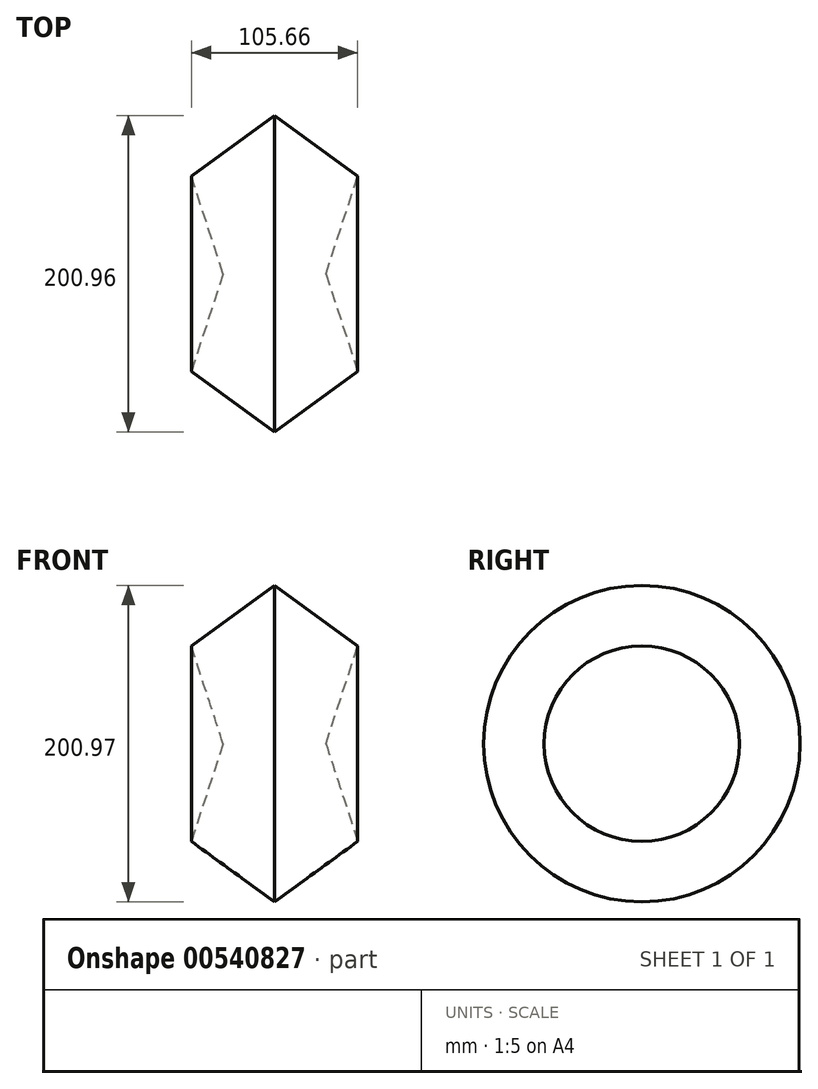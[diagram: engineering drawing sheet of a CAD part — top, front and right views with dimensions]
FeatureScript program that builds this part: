
annotation { "Feature Type Name" : "Feature", "Feature Type Description" : "" }
export const myFeature = defineFeature(function(context is Context, id is Id, definition is map)
    precondition{}
    {
        {
            var Q0;
            Q0=qCreatedBy(makeId("Front.planeOp"),FACE);
            var sketch = newSketch(context, id + "F0", { "sketchPlane" : qUnion([Q0])});
            skCircle(sketch, "E0.cCircle", {"center": v(0, 0) * mm, "radius": 44.94 * mm, "construction": true});
            skLineSegment(sketch, "E0.0", {"start": v(0, 55.55) * mm, "end": v(52.83, 17.16) * mm});
            skLineSegment(sketch, "E0.1", {"start": v(52.83, 17.16) * mm, "end": v(32.65, -44.94) * mm});
            skLineSegment(sketch, "E0.2", {"start": v(32.65, -44.94) * mm, "end": v(-32.65, -44.94) * mm});
            skLineSegment(sketch, "E0.3", {"start": v(-32.65, -44.94) * mm, "end": v(-52.83, 17.16) * mm});
            skLineSegment(sketch, "E0.4", {"start": v(-52.83, 17.16) * mm, "end": v(0, 55.55) * mm});
            skPoint(sketch, "E0.0.midPoint", {"position": v(26.41, 36.36) * mm});
            skSolve(sketch);
        }
        {
            var Q0;
            Q0=makeQuery(id+"F0.imprint","IMPRINT",FACE,{"disambiguationData":[TD([[makeQuery(id+"F0.imprint","IMPRINT",EDGE,{"derivedFrom":sQuery(id+"F0.wireOp",EDGE,"E0.0")}),-1.0]])]});
            var Q1;
            Q1=sQuery(id+"F0.wireOp",EDGE,"E0.2");
            revolve(context, id + "F1", {"entities" : qUnion([Q0]), "axis" : qUnion([Q1]), "revolveType" : RevolveType.FULL});
        }
    });
